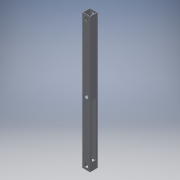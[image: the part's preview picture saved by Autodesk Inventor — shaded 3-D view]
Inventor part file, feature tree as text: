
AUTODESK INVENTOR PART (.ipt)
format: ipt  version: 2016 (Build 200138000, 138)  size: 138,240 bytes
history: native  units: in
note: dims shown in document units (in); Inventor stores cm internally (conversion verified against a paired STEP export)
features: extrude x5, sketch x5
ambient origin geometry x8: Origin, YZ Plane, XZ Plane, XY Plane, X Axis, Y Axis, Z Axis, Center Point
bodies: Solid1 (feature_tree)
feature tree (10):
  extrude  "Extrusion1"  Depth=1.0in
  extrude  "Extrusion2"  Depth=17.5in TaperAngle=0.0deg
  extrude  "Extrusion4"  Depth=0.5in
  extrude  "Extrusion5"  Depth=1.0in
  extrude  "Extrusion6"  Depth=1.0in
  sketch  "Sketch1"  dims[d0=1.0in d1=1.0in]
  sketch  "Sketch2"  dims[d2=0.0625in d3=17.5in d4=0.0in]
  sketch  "Sketch4"  dims[d5=0.5in d6=0.5in]
  sketch  "Sketch5"  dims[d7=1.0in d8=0.0in d17=0.5in]
  sketch  "Sketch6"  dims[d18=0.5in d19=0.5in d20=1.0in d21=0.0in d22=0.5in d23=0.5in d24=9.25in d25=1.0in d26=0.0in d28=0.2in d29=0.2in d30=6.945in d31=1.0in d32=0.0in d33=1.0in]
